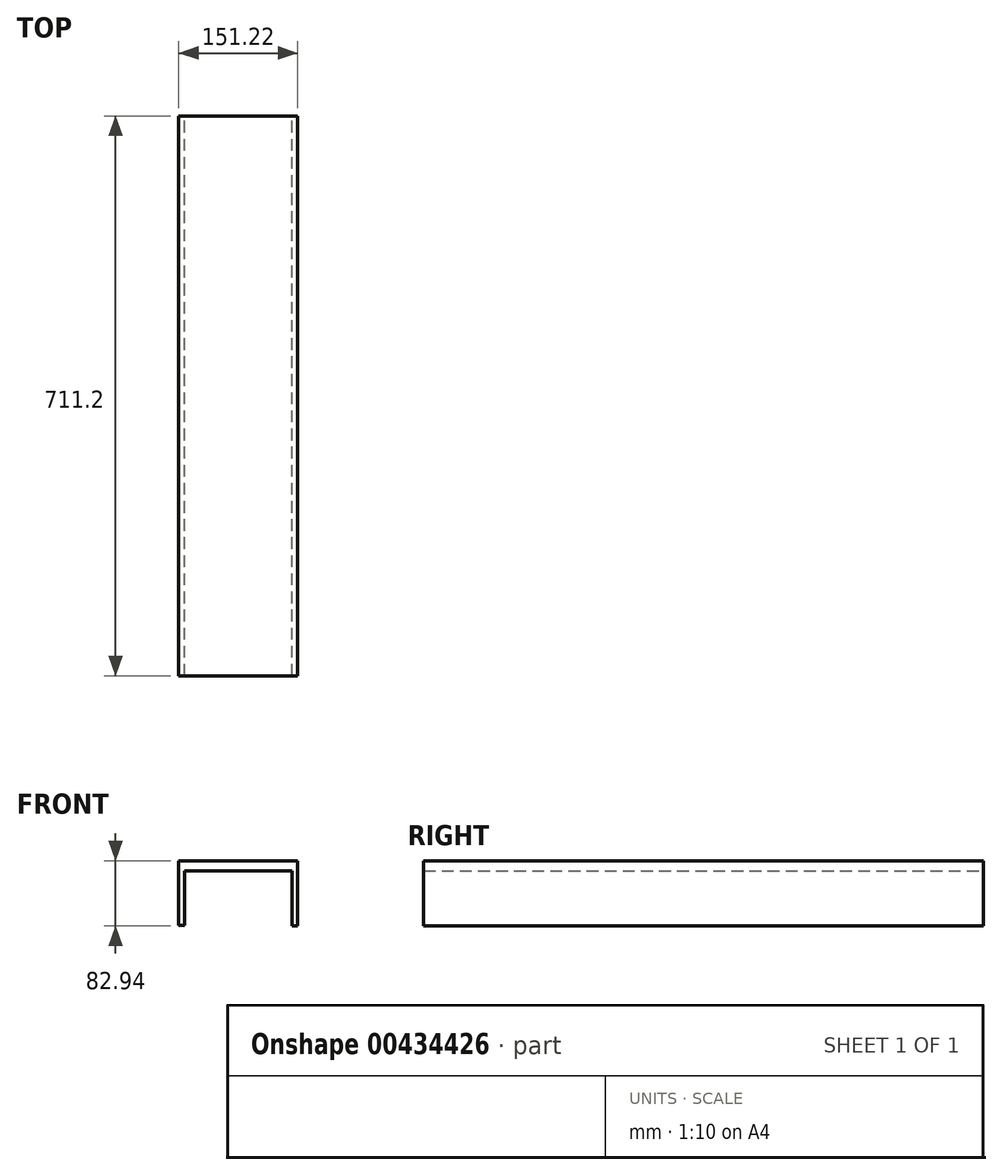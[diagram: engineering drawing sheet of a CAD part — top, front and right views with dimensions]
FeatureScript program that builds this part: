
annotation { "Feature Type Name" : "Feature", "Feature Type Description" : "" }
export const myFeature = defineFeature(function(context is Context, id is Id, definition is map)
    precondition{}
    {
        {
            var Q0;
            Q0=qCreatedBy(makeId("Front.planeOp"),FACE);
            var sketch = newSketch(context, id + "F0", { "sketchPlane" : qUnion([Q0])});
            skLineSegment(sketch, "E0.bottom", {"start": v(-75.6, 6.54) * mm, "end": v(75.6, 6.54) * mm});
            skLineSegment(sketch, "E0.top", {"start": v(-75.6, -6.54) * mm, "end": v(75.6, -6.54) * mm});
            skLineSegment(sketch, "E0.left", {"start": v(-75.6, 6.54) * mm, "end": v(-75.6, -6.54) * mm});
            skLineSegment(sketch, "E0.right", {"start": v(75.6, 6.54) * mm, "end": v(75.6, -6.54) * mm});
            skPoint(sketch, "E0.middle", {"position": v(0, 0) * mm});
            skLineSegment(sketch, "E1.bottom", {"start": v(-75.6, -6.54) * mm, "end": v(-68.27, -6.54) * mm});
            skLineSegment(sketch, "E1.top", {"start": v(-75.6, -75.77) * mm, "end": v(-68.27, -75.77) * mm});
            skLineSegment(sketch, "E1.left", {"start": v(-75.6, -6.54) * mm, "end": v(-75.6, -75.77) * mm});
            skLineSegment(sketch, "E1.right", {"start": v(-68.27, -6.54) * mm, "end": v(-68.27, -75.77) * mm});
            skLineSegment(sketch, "E2.bottom", {"start": v(75.6, -6.54) * mm, "end": v(68.27, -6.54) * mm});
            skLineSegment(sketch, "E2.top", {"start": v(75.6, -76.4) * mm, "end": v(68.27, -76.4) * mm});
            skLineSegment(sketch, "E2.left", {"start": v(75.6, -6.54) * mm, "end": v(75.6, -76.4) * mm});
            skLineSegment(sketch, "E2.right", {"start": v(68.27, -6.54) * mm, "end": v(68.27, -76.4) * mm});
            skSolve(sketch);
        }
        {
            var Q0;
            Q0 = qSketchRegion(id + "F0", true);
            extrude(context, id + "F1", {"entities" : qUnion([Q0]), "depth" : 711.2 * mm});
        }
    });
